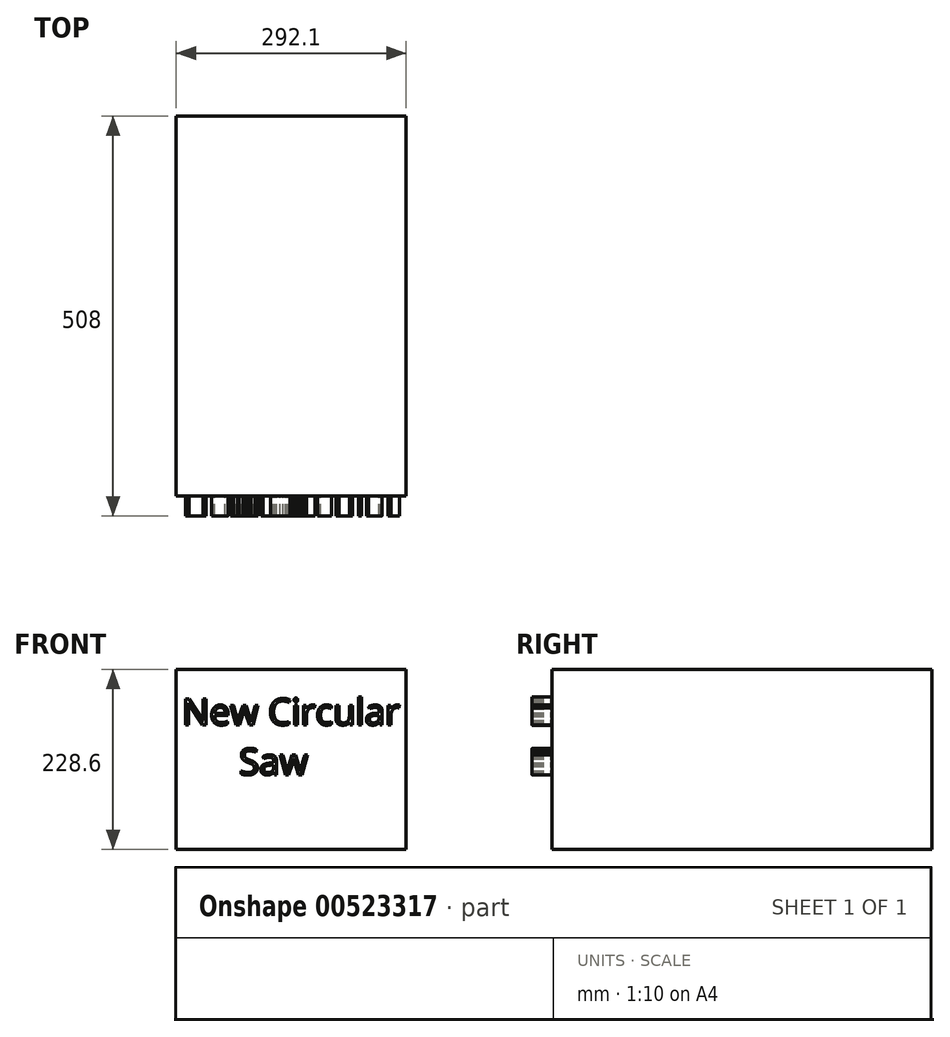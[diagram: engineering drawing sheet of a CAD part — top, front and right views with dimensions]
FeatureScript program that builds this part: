
annotation { "Feature Type Name" : "Feature", "Feature Type Description" : "" }
export const myFeature = defineFeature(function(context is Context, id is Id, definition is map)
    precondition{}
    {
        {
            var Q0;
            Q0=qCreatedBy(makeId("Front.planeOp"),FACE);
            var sketch = newSketch(context, id + "F0", { "sketchPlane" : qUnion([Q0])});
            skLineSegment(sketch, "E0.bottom", {"start": v(146.05, 114.3) * mm, "end": v(-146.05, 114.3) * mm});
            skLineSegment(sketch, "E0.top", {"start": v(146.05, -114.3) * mm, "end": v(-146.05, -114.3) * mm});
            skLineSegment(sketch, "E0.left", {"start": v(146.05, 114.3) * mm, "end": v(146.05, -114.3) * mm});
            skLineSegment(sketch, "E0.right", {"start": v(-146.05, 114.3) * mm, "end": v(-146.05, -114.3) * mm});
            skPoint(sketch, "E0.middle", {"position": v(0, 0) * mm});
            skSolve(sketch);
        }
        {
            var Q0;
            Q0=makeQuery(id+"F0.imprint","IMPRINT",FACE,{"disambiguationData":[TD([[makeQuery(id+"F0.imprint","IMPRINT",EDGE,{"derivedFrom":sQuery(id+"F0.wireOp",EDGE,"E0.bottom")}),1.0]])]});
            extrude(context, id + "F1", {"entities" : qUnion([Q0]), "depth" : 482.6 * mm, "offsetDistance" : 25.4 * mm});
        }
        {
            var Q0;
            Q0=makeQuery(id+"F1.opExtrude","CAP_FACE",FACE,{"disambiguationData":[OSD([sQuery(id+"F0.wireOp",EDGE,"E0.bottom"),sQuery(id+"F0.wireOp",EDGE,"E0.top"),sQuery(id+"F0.wireOp",EDGE,"E0.left"),sQuery(id+"F0.wireOp",EDGE,"E0.right")])],"isStart":false});
            var sketch = newSketch(context, id + "F2", { "sketchPlane" : qUnion([Q0])});
            skText(sketch, "E1", { "text": "New Circular\n      Saw", "fontName": "OpenSans-Regular.ttf"});
            const initialGuessF2  = {"E1": [-0.13873, 0.0439, 1, 0, 0.03351]};
            skSetInitialGuess(sketch, initialGuessF2);
            skSolve(sketch);
        }
        {
            var Q0;
            Q0 = qSketchRegion(id + "F2", true);
            extrude(context, id + "F3", {"entities" : qUnion([Q0]), "operationType" : NewBodyOperationType.ADD, "depth" : 25.4 * mm, "offsetDistance" : 25.4 * mm});
        }
    });
